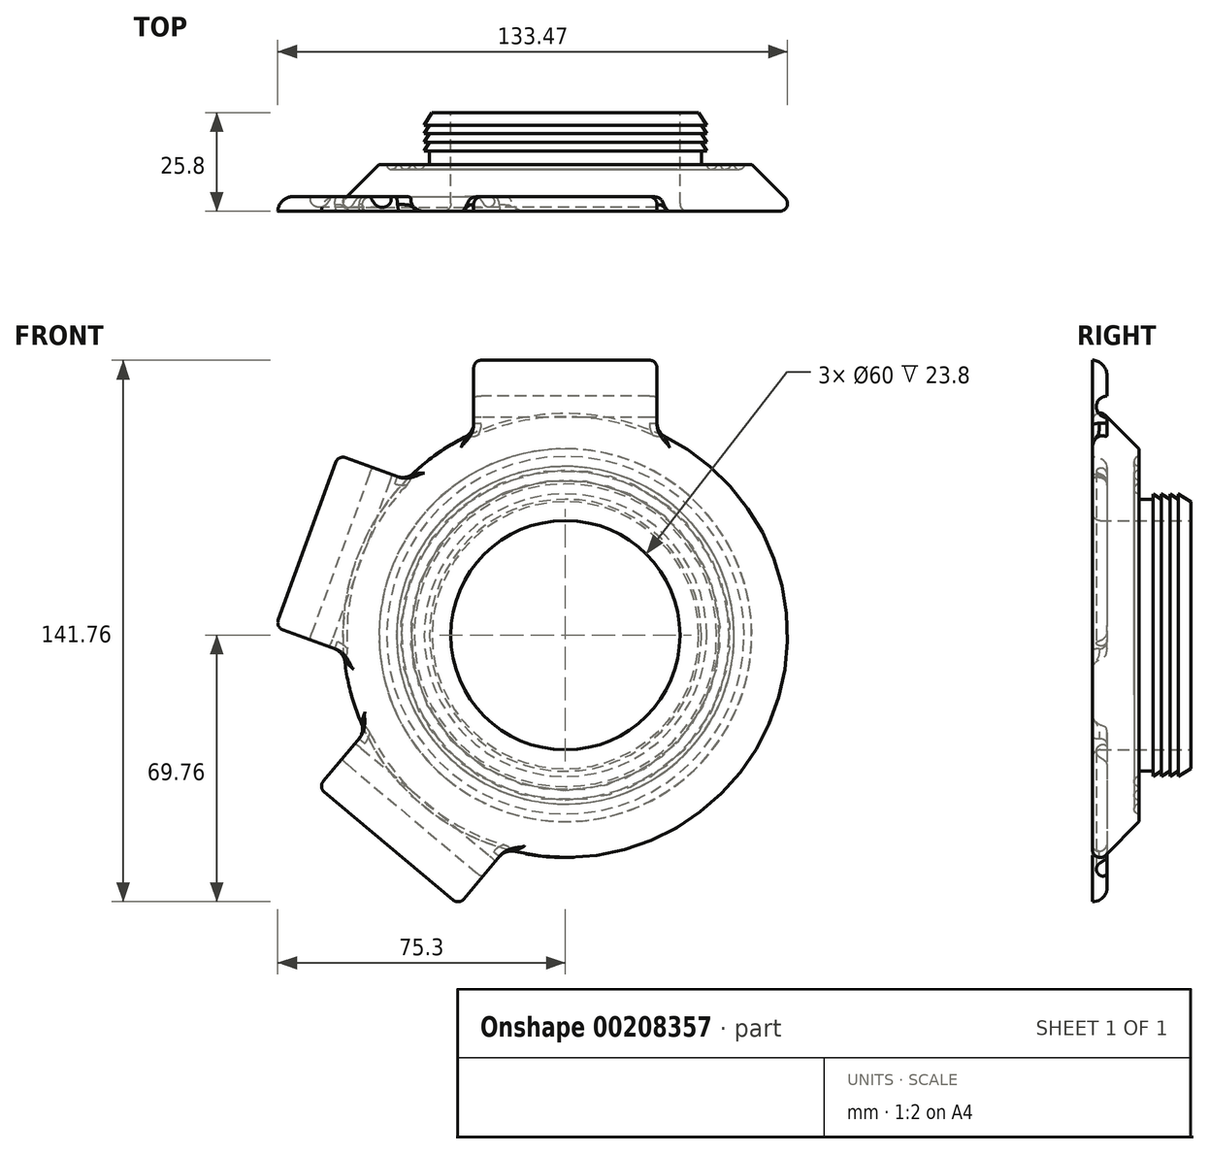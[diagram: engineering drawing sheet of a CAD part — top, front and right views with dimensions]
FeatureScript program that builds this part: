
annotation { "Feature Type Name" : "Feature", "Feature Type Description" : "" }
export const myFeature = defineFeature(function(context is Context, id is Id, definition is map)
    precondition{}
    {
        {
            var Q0;
            Q0=qCreatedBy(makeId("Right.planeOp"),FACE);
            var sketch = newSketch(context, id + "F0", { "sketchPlane" : qUnion([Q0])});
            skLineSegment(sketch, "E0", {"start": v(0, 61) * mm, "end": v(12.2, 48.8) * mm});
            skLineSegment(sketch, "E1", {"start": v(12.2, 48.8) * mm, "end": v(12.2, 37.2) * mm});
            skLineSegment(sketch, "E2", {"start": v(12.2, 37.2) * mm, "end": v(25.8, 37.2) * mm});
            skLineSegment(sketch, "E3", {"start": v(25.8, 37.2) * mm, "end": v(25.8, 30) * mm});
            skLineSegment(sketch, "E4", {"start": v(25.8, 30) * mm, "end": v(0, 30) * mm});
            skLineSegment(sketch, "E5", {"start": v(0, 30) * mm, "end": v(0, 61) * mm});
            skSolve(sketch);
        }
        {
            var Q0;
            Q0=qCreatedBy(makeId("Right.planeOp"),FACE);
            var sketch = newSketch(context, id + "F1", { "sketchPlane" : qUnion([Q0])});
            skLineSegment(sketch, "E6", {"start": v(52.48, 0) * mm, "end": v(-53.59, 0) * mm});
            skSolve(sketch);
        }
        {
            var Q0;
            Q0 = qSketchRegion(id + "F0", true);
            var Q1;
            Q1=sQuery(id+"F1.wireOp",EDGE,"E6");
            revolve(context, id + "F2", {"entities" : qUnion([Q0]), "axis" : qUnion([Q1]), "revolveType" : RevolveType.FULL});
        }
        {
            var Q0;
            Q0=makeQuery(id+"F2.opRevolve","SWEPT_EDGE",EDGE,{"disambiguationData":[OSD([sQuery(id+"F0.wireOp",EDGE,"E0"),sQuery(id+"F0.wireOp",EDGE,"E5")])]});
            fillet(context, id + "F3", {"entities" : qUnion([Q0]), "radius" : 2 * mm, "allowEdgeOverflow" : false});
        }
        {
            var Q0;
            Q0=qCreatedBy(makeId("Right.planeOp"),FACE);
            var sketch = newSketch(context, id + "F4", { "sketchPlane" : qUnion([Q0])});
            skLineSegment(sketch, "E7", {"start": v(25.8, 34.93) * mm, "end": v(22.5, 37) * mm});
            skLineSegment(sketch, "E8", {"start": v(22.5, 37) * mm, "end": v(22.5, 35.6) * mm});
            skLineSegment(sketch, "E9", {"start": v(22.5, 35.6) * mm, "end": v(20.27, 37) * mm});
            skLineSegment(sketch, "E10", {"start": v(20.27, 37) * mm, "end": v(20.27, 35.6) * mm});
            skLineSegment(sketch, "E11", {"start": v(20.27, 35.6) * mm, "end": v(18.03, 37) * mm});
            skLineSegment(sketch, "E12", {"start": v(18.03, 37) * mm, "end": v(18.03, 35.6) * mm});
            skLineSegment(sketch, "E13", {"start": v(18.03, 35.6) * mm, "end": v(15.8, 37) * mm});
            skLineSegment(sketch, "E14", {"start": v(15.8, 37) * mm, "end": v(15.8, 35.6) * mm});
            skLineSegment(sketch, "E15", {"start": v(15.8, 35.6) * mm, "end": v(12.2, 35.6) * mm});
            skLineSegment(sketch, "E16", {"start": v(12.2, 35.6) * mm, "end": v(12.2, 38.87) * mm});
            skLineSegment(sketch, "E17", {"start": v(12.2, 38.87) * mm, "end": v(25.8, 38.87) * mm});
            skLineSegment(sketch, "E18", {"start": v(25.8, 38.87) * mm, "end": v(25.8, 34.93) * mm});
            skSolve(sketch);
        }
        {
            var Q0;
            Q0 = qSketchRegion(id + "F4", true);
            var Q1;
            Q1=makeQuery(id+"F2.opRevolve","SWEPT_FACE",FACE,{"disambiguationData":[OSD([sQuery(id+"F0.wireOp",EDGE,"E2")])]});
            revolve(context, id + "F5", {"operationType" : NewBodyOperationType.REMOVE, "entities" : qUnion([Q0]), "axis" : qUnion([Q1]), "revolveType" : RevolveType.FULL, "oppositeDirection" : true});
        }
        {
            var Q0;
            Q0=qCreatedBy(makeId("Right.planeOp"),FACE);
            var sketch = newSketch(context, id + "F6", { "sketchPlane" : qUnion([Q0])});
            skArc(sketch, "E19", {"start": v(12.2, 37) * mm, "mid": v(10.9, 38.3) * mm, "end": v(12.2, 39.6) * mm});
            skArc(sketch, "E20.1.0.0", {"start": v(12.2, 40.6) * mm, "mid": v(10.9, 41.9) * mm, "end": v(12.2, 43.2) * mm});
            skArc(sketch, "E20.2.0.0", {"start": v(12.2, 44.2) * mm, "mid": v(10.9, 45.5) * mm, "end": v(12.2, 46.8) * mm});
            skLineSegment(sketch, "E20.direction1", {"start": v(12.2, 39.6) * mm, "end": v(12.2, 43.2) * mm, "construction": true});
            skLineSegment(sketch, "E21", {"start": v(12.2, 46.8) * mm, "end": v(12.2, 44.2) * mm});
            skLineSegment(sketch, "E22", {"start": v(12.2, 43.2) * mm, "end": v(12.2, 40.6) * mm});
            skLineSegment(sketch, "E23", {"start": v(12.2, 39.6) * mm, "end": v(12.2, 37) * mm});
            skSolve(sketch);
        }
        {
            var Q0;
            Q0=qCreatedBy(makeId("Right.planeOp"),FACE);
            var sketch = newSketch(context, id + "F7", { "sketchPlane" : qUnion([Q0])});
            skLineSegment(sketch, "E24", {"start": v(-32.77, 0) * mm, "end": v(46.17, 0) * mm});
            skSolve(sketch);
        }
        {
            var Q0;
            Q0 = qSketchRegion(id + "F6", true);
            var Q1;
            Q1=sQuery(id+"F7.wireOp",EDGE,"E24");
            revolve(context, id + "F8", {"operationType" : NewBodyOperationType.REMOVE, "entities" : qUnion([Q0]), "axis" : qUnion([Q1]), "revolveType" : RevolveType.FULL});
        }
        {
            var Q0;
            Q0=qCreatedBy(makeId("Front.planeOp"),FACE);
            var sketch = newSketch(context, id + "F9", { "sketchPlane" : qUnion([Q0])});
            skLineSegment(sketch, "E25", {"start": v(0, 50.79) * mm, "end": v(24, 50.79) * mm});
            skLineSegment(sketch, "E26", {"start": v(24, 50.79) * mm, "end": v(24, 72) * mm});
            skLineSegment(sketch, "E27", {"start": v(24, 72) * mm, "end": v(0, 72) * mm});
            skLineSegment(sketch, "E28.MirrorCS", {"start": v(0, 50.79) * mm, "end": v(-24, 50.79) * mm});
            skLineSegment(sketch, "E29.MirrorCS", {"start": v(-24, 50.79) * mm, "end": v(-24, 72) * mm});
            skLineSegment(sketch, "E30.MirrorCS", {"start": v(-24, 72) * mm, "end": v(0, 72) * mm});
            skPoint(sketch, "E31.center", {"position": v(0, 0) * mm});
            skSolve(sketch);
        }
        {
            var Q0;
            Q0 = qSketchRegion(id + "F9", true);
            extrude(context, id + "F10", {"entities" : qUnion([Q0]), "operationType" : NewBodyOperationType.ADD, "oppositeDirection" : true, "depth" : 3.8 * mm});
        }
        {
            var Q0;
            Q0=makeQuery(id+"F10.boolean.opBoolean","INTERSECT",EDGE,{"derivedFrom":[makeQuery(id+"F3.opFillet","BLEND_FACE",FACE,{"disambiguationData":[OSD([sQuery(id+"F0.wireOp",EDGE,"E0"),sQuery(id+"F0.wireOp",EDGE,"E5")])]}),makeQuery(id+"F10.opExtrude","SWEPT_FACE",FACE,{"disambiguationData":[OSD([sQuery(id+"F9.wireOp",EDGE,"E29.MirrorCS")])]})]});
            var Q1;
            Q1=makeQuery(id+"F10.boolean.opBoolean","INTERSECT",EDGE,{"derivedFrom":[makeQuery(id+"F3.opFillet","BLEND_FACE",FACE,{"disambiguationData":[OSD([sQuery(id+"F0.wireOp",EDGE,"E0"),sQuery(id+"F0.wireOp",EDGE,"E5")])]}),makeQuery(id+"F10.opExtrude","SWEPT_FACE",FACE,{"disambiguationData":[OSD([sQuery(id+"F9.wireOp",EDGE,"E26")])]})]});
            fillet(context, id + "F11", {"entities" : qUnion([Q0, Q1]), "radius" : 4 * mm, "tangentPropagation" : true, "allowEdgeOverflow" : false});
        }
        {
            var Q0;
            Q0=makeQuery(id+"F10.opExtrude","CAP_EDGE",EDGE,{"disambiguationData":[OSD([sQuery(id+"F9.wireOp",EDGE,"E27"),sQuery(id+"F9.wireOp",EDGE,"E30.MirrorCS")])],"isStart":false});
            fillet(context, id + "F12", {"entities" : qUnion([Q0]), "radius" : 4 * mm, "tangentPropagation" : true, "allowEdgeOverflow" : false});
        }
        {
            var Q0;
            Q0=makeQuery(id+"F10.opExtrude","SWEPT_FACE",FACE,{"disambiguationData":[OSD([sQuery(id+"F9.wireOp",EDGE,"E29.MirrorCS")])]});
            var sketch = newSketch(context, id + "F13", { "sketchPlane" : qUnion([Q0])});
            skArc(sketch, "E32", {"start": v(-3.8, 57) * mm, "mid": v(-1, 59.8) * mm, "end": v(-3.8, 62.6) * mm});
            skLineSegment(sketch, "E33", {"start": v(-3.8, 57) * mm, "end": v(-3.8, 62.6) * mm});
            skSolve(sketch);
        }
        {
            var Q0;
            Q0=makeQuery(id+"F13.imprint","IMPRINT",FACE,{"disambiguationData":[TD([[makeQuery(id+"F13.imprint","IMPRINT",EDGE,{"derivedFrom":sQuery(id+"F13.wireOp",EDGE,"E32")}),1.0]])]});
            var Q1;
            Q1=sQuery(id+"F13.wireOp",EDGE,"E32");
            var Q2;
            Q2=sQuery(id+"F13.wireOp",EDGE,"E33");
            extrude(context, id + "F14", {"entities" : qUnion([Q0]), "operationType" : NewBodyOperationType.REMOVE, "surfaceEntities" : qUnion([Q1, Q2]), "endBound" : BoundingType.THROUGH_ALL, "oppositeDirection" : true, "depth" : 25 * mm});
        }
        {
            var Q0;
            {var subQ0=sQuery(id+"F9.wireOp",EDGE,"E30.MirrorCS");var subQ1=sQuery(id+"F9.wireOp",EDGE,"E29.MirrorCS");var subQ2=sQuery(id+"F9.wireOp",EDGE,"E27");Q0=makeQuery(id+"F14.boolean.opBoolean","SPLIT",EDGE,{"disambiguationData":[TD([makeQuery(id+"F12.opFillet","BLEND_FACE",FACE,{"disambiguationData":[OSD([subQ2,subQ0])]})])],"derivedFrom":makeQuery(id+"F10.opExtrude","CAP_EDGE",EDGE,{"disambiguationData":[OSD([subQ1])],"isStart":false})});}
            var Q1;
            {var subQ0=sQuery(id+"F9.wireOp",EDGE,"E29.MirrorCS");Q1=makeQuery(id+"F14.boolean.opBoolean","SPLIT",EDGE,{"disambiguationData":[TD([makeQuery(id+"F11.opFillet","BLEND_FACE",FACE,{"disambiguationData":[OSD([sQuery(id+"F0.wireOp",EDGE,"E0"),sQuery(id+"F0.wireOp",EDGE,"E5"),subQ0])]})])],"derivedFrom":makeQuery(id+"F10.opExtrude","CAP_EDGE",EDGE,{"disambiguationData":[OSD([subQ0])],"isStart":false})});}
            var Q2;
            {var subQ0=sQuery(id+"F9.wireOp",EDGE,"E30.MirrorCS");var subQ1=sQuery(id+"F9.wireOp",EDGE,"E27");var subQ2=sQuery(id+"F9.wireOp",EDGE,"E26");Q2=makeQuery(id+"F14.boolean.opBoolean","SPLIT",EDGE,{"disambiguationData":[TD([makeQuery(id+"F12.opFillet","BLEND_FACE",FACE,{"disambiguationData":[OSD([subQ1,subQ0])]})])],"derivedFrom":makeQuery(id+"F10.opExtrude","CAP_EDGE",EDGE,{"disambiguationData":[OSD([subQ2])],"isStart":false})});}
            var Q3;
            {var subQ0=sQuery(id+"F9.wireOp",EDGE,"E26");Q3=makeQuery(id+"F14.boolean.opBoolean","SPLIT",EDGE,{"disambiguationData":[TD([makeQuery(id+"F11.opFillet","BLEND_FACE",FACE,{"disambiguationData":[OSD([sQuery(id+"F0.wireOp",EDGE,"E0"),sQuery(id+"F0.wireOp",EDGE,"E5"),subQ0])]})])],"derivedFrom":makeQuery(id+"F10.opExtrude","CAP_EDGE",EDGE,{"disambiguationData":[OSD([subQ0])],"isStart":false})});}
            fillet(context, id + "F15", {"entities" : qUnion([Q0, Q1, Q2, Q3]), "radius" : 2 * mm, "tangentPropagation" : true, "allowEdgeOverflow" : false});
        }
        {
            var Q0;
            Q0=makeQuery(id+"F2.opRevolve","SWEPT_EDGE",EDGE,{"disambiguationData":[OSD([sQuery(id+"F0.wireOp",EDGE,"E4"),sQuery(id+"F0.wireOp",EDGE,"E5")])]});
            fillet(context, id + "F16", {"entities" : qUnion([Q0]), "radius" : 2 * mm, "tangentPropagation" : true, "allowEdgeOverflow" : false});
        }
        {
            var Q0;
            Q0=makeQuery(id+"F2.opRevolve","SWEPT_BODY",BODY,{"disambiguationData":[OSD([sQuery(id+"F0.wireOp",EDGE,"E0"),sQuery(id+"F0.wireOp",EDGE,"E1"),sQuery(id+"F0.wireOp",EDGE,"E2"),sQuery(id+"F0.wireOp",EDGE,"E3"),sQuery(id+"F0.wireOp",EDGE,"E4"),sQuery(id+"F0.wireOp",EDGE,"E5")])]});
            var Q1;
            Q1=makeQuery(id+"F2.opRevolve","SWEPT_FACE",FACE,{"disambiguationData":[OSD([sQuery(id+"F0.wireOp",EDGE,"E4")])]});
            circularPattern(context, id + "F17", {"entities" : qUnion([Q0]), "axis" : qUnion([Q1]), "angle" : 140 * degree, "instanceCount" : 3, "equalSpace" : true});
        }
    });
